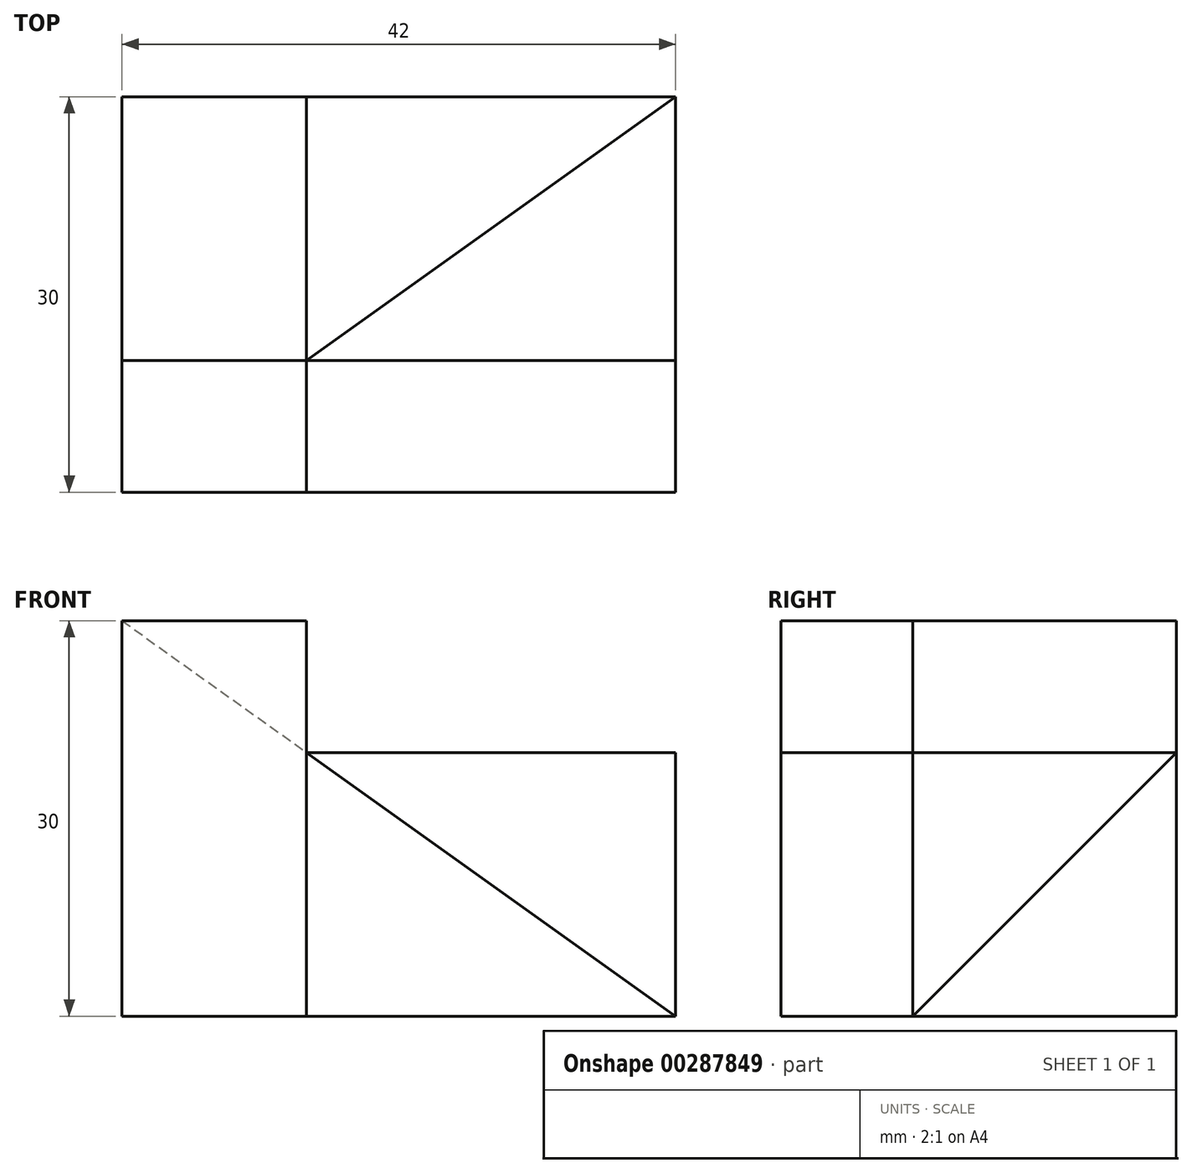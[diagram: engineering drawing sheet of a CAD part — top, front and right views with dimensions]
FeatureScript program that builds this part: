
annotation { "Feature Type Name" : "Feature", "Feature Type Description" : "" }
export const myFeature = defineFeature(function(context is Context, id is Id, definition is map)
    precondition{}
    {
        {
            var Q0;
            Q0=qCreatedBy(makeId("Front.planeOp"),FACE);
            var sketch = newSketch(context, id + "F0", { "sketchPlane" : qUnion([Q0])});
            skLineSegment(sketch, "E0.bottom", {"start": v(0, 0) * mm, "end": v(42, 0) * mm});
            skLineSegment(sketch, "E0.top", {"start": v(0, 30) * mm, "end": v(42, 30) * mm});
            skLineSegment(sketch, "E0.left", {"start": v(0, 0) * mm, "end": v(0, 30) * mm});
            skLineSegment(sketch, "E0.right", {"start": v(42, 0) * mm, "end": v(42, 30) * mm});
            skLineSegment(sketch, "E1.bottom", {"start": v(42, 30) * mm, "end": v(14, 30) * mm});
            skLineSegment(sketch, "E1.top", {"start": v(42, 20) * mm, "end": v(14, 20) * mm});
            skLineSegment(sketch, "E1.left", {"start": v(42, 30) * mm, "end": v(42, 20) * mm});
            skLineSegment(sketch, "E1.right", {"start": v(14, 30) * mm, "end": v(14, 20) * mm});
            skSolve(sketch);
        }
        {
            var Q0;
            Q0=makeQuery(id+"F0.imprint","IMPRINT",FACE,{"disambiguationData":[TD([[makeQuery(id+"F0.imprint","IMPRINT",EDGE,{"derivedFrom":sQuery(id+"F0.wireOp",EDGE,"E0.bottom")}),1.0]])]});
            extrude(context, id + "F1", {"entities" : qUnion([Q0]), "depth" : 30 * mm});
        }
        {
            var Q0;
            Q0=makeQuery(id+"F1.opExtrude","CAP_FACE",FACE,{"disambiguationData":[OSD([sQuery(id+"F0.wireOp",EDGE,"E0.bottom"),sQuery(id+"F0.wireOp",EDGE,"E0.top"),sQuery(id+"F0.wireOp",EDGE,"E0.left"),sQuery(id+"F0.wireOp",EDGE,"E0.right"),sQuery(id+"F0.wireOp",EDGE,"E1.top"),sQuery(id+"F0.wireOp",EDGE,"E1.right")])],"isStart":true});
            var sketch = newSketch(context, id + "F2", { "sketchPlane" : qUnion([Q0])});
            skLineSegment(sketch, "E2", {"start": v(0, 30) * mm, "end": v(-14, 20) * mm});
            skSolve(sketch);
        }
        {
            var Q0;
            Q0=makeQuery(id+"F2.imprint","IMPRINT",FACE,{"disambiguationData":[TD([[makeQuery(id+"F2.imprint","IMPRINT",EDGE,{"derivedFrom":sQuery(id+"F2.wireOp",EDGE,"E2")}),-1.0]])]});
            extrude(context, id + "F3", {"entities" : qUnion([Q0]), "operationType" : NewBodyOperationType.REMOVE, "flatOperationType" : FlatOperationType.REMOVE, "oppositeDirection" : true, "offsetDistance" : 25 * mm, "depth" : 20 * mm, "domain" : OperationDomain.MODEL});
        }
        {
            var Q0;
            Q0=makeQuery(id+"F1.opExtrude","CAP_FACE",FACE,{"disambiguationData":[OSD([sQuery(id+"F0.wireOp",EDGE,"E0.bottom"),sQuery(id+"F0.wireOp",EDGE,"E0.top"),sQuery(id+"F0.wireOp",EDGE,"E0.left"),sQuery(id+"F0.wireOp",EDGE,"E0.right"),sQuery(id+"F0.wireOp",EDGE,"E1.top"),sQuery(id+"F0.wireOp",EDGE,"E1.right")])],"isStart":false});
            var sketch = newSketch(context, id + "F4", { "sketchPlane" : qUnion([Q0])});
            skLineSegment(sketch, "E3", {"start": v(14, 20) * mm, "end": v(42, 0) * mm});
            skLineSegment(sketch, "E4", {"start": v(14, 20) * mm, "end": v(14, 0) * mm});
            skSolve(sketch);
        }
        {
            var Q0;
            Q0=makeQuery(id+"F4.imprint","IMPRINT",FACE,{"disambiguationData":[TD([[makeQuery(id+"F4.imprint","IMPRINT",EDGE,{"derivedFrom":sQuery(id+"F4.wireOp",EDGE,"E3")}),1.0]])]});
            extrude(context, id + "F5", {"entities" : qUnion([Q0]), "operationType" : NewBodyOperationType.REMOVE, "flatOperationType" : FlatOperationType.REMOVE, "oppositeDirection" : true, "offsetDistance" : 25 * mm, "depth" : 10 * mm, "domain" : OperationDomain.MODEL});
        }
        {
            var Q0;
            {var subQ0=sQuery(id+"F0.wireOp",EDGE,"E1.right");var subQ1=sQuery(id+"F0.wireOp",EDGE,"E1.top");Q0=makeQuery(id+"F5.boolean.opBoolean","MERGE",VERTEX,{"derivedFrom":[makeQuery(id+"F3.boolean.opBoolean","COPY",VERTEX,{"derivedFrom":makeQuery(id+"F3.opExtrude","CAP_VERTEX",VERTEX,{"disambiguationData":[OSD([subQ1,subQ0,sQuery(id+"F2.wireOp",EDGE,"E2")])],"isStart":false})}),makeQuery(id+"F5.opExtrude","CAP_VERTEX",VERTEX,{"disambiguationData":[OSD([subQ1,subQ0,sQuery(id+"F4.wireOp",EDGE,"E3")])],"isStart":false})]});}
            var Q1;
            Q1=makeQuery(id+"F1.opExtrude","CAP_VERTEX",VERTEX,{"disambiguationData":[OSD([sQuery(id+"F0.wireOp",EDGE,"E0.right"),sQuery(id+"F0.wireOp",EDGE,"E1.top"),sQuery(id+"F0.wireOp",EDGE,"E1.left")])],"isStart":true});
            var Q2;
            Q2=makeQuery(id+"F5.boolean.opBoolean","COPY",VERTEX,{"derivedFrom":makeQuery(id+"F5.opExtrude","CAP_VERTEX",VERTEX,{"disambiguationData":[OSD([sQuery(id+"F0.wireOp",EDGE,"E0.bottom"),sQuery(id+"F0.wireOp",EDGE,"E0.right"),sQuery(id+"F4.wireOp",EDGE,"E3")])],"isStart":false})});
            cPlane(context, id + "F6", {"entities" : qUnion([Q0, Q1, Q2]), "cplaneType" : CPlaneType.THREE_POINT, "offset" : 25 * mm, "width" : 150 * mm, "height" : 150 * mm});
        }
        {
            var Q0;
            Q0=qCreatedBy(id+"F6.planeOp",FACE);
            var sketch = newSketch(context, id + "F7", { "sketchPlane" : qUnion([Q0])});
            skPoint(sketch, "E5.0", {"position": v(-0.26, 0) * mm});
            skPoint(sketch, "E6.0", {"position": v(31.11, 14.14) * mm});
            skPoint(sketch, "E7.0", {"position": v(31.11, -14.14) * mm});
            skLineSegment(sketch, "E8", {"start": v(-0.26, 0) * mm, "end": v(31.11, 14.14) * mm});
            skLineSegment(sketch, "E9", {"start": v(31.11, -14.14) * mm, "end": v(31.11, 14.14) * mm});
            skLineSegment(sketch, "E10", {"start": v(-0.26, 0) * mm, "end": v(31.11, -14.14) * mm});
            skSolve(sketch);
        }
        {
            var Q0;
            Q0 = qSketchRegion(id + "F7", true);
            extrude(context, id + "F8", {"entities" : qUnion([Q0]), "operationType" : NewBodyOperationType.REMOVE, "endBound" : BoundingType.THROUGH_ALL, "depth" : 25 * mm});
        }
        {
            var Q0;
            Q0 = qSketchRegion(id + "F4", true);
            var Q1;
            Q1=makeQuery(id+"F4.imprint","IMPRINT",FACE,{"disambiguationData":[TD([[makeQuery(id+"F4.imprint","IMPRINT",EDGE,{"derivedFrom":sQuery(id+"F4.wireOp",EDGE,"E3")}),1.0]])]});
            var Q2;
            {var subQ0=sQuery(id+"F0.wireOp",EDGE,"E1.right");var subQ1=sQuery(id+"F0.wireOp",EDGE,"E1.top");Q2=makeQuery(id+"F8.boolean.opBoolean","MERGE",VERTEX,{"derivedFrom":[makeQuery(id+"F5.boolean.opBoolean","MERGE",VERTEX,{"derivedFrom":[makeQuery(id+"F3.boolean.opBoolean","COPY",VERTEX,{"derivedFrom":makeQuery(id+"F3.opExtrude","CAP_VERTEX",VERTEX,{"disambiguationData":[OSD([subQ1,subQ0,sQuery(id+"F2.wireOp",EDGE,"E2")])],"isStart":false})}),makeQuery(id+"F5.opExtrude","CAP_VERTEX",VERTEX,{"disambiguationData":[OSD([subQ1,subQ0,sQuery(id+"F4.wireOp",EDGE,"E3"),sQuery(id+"F4.wireOp",EDGE,"E4")])],"isStart":false})]}),makeQuery(id+"F8.opExtrude","CAP_VERTEX",VERTEX,{"disambiguationData":[OSD([sQuery(id+"F7.wireOp",EDGE,"E8"),sQuery(id+"F7.wireOp",EDGE,"E10")])],"isStart":true})]});}
            extrude(context, id + "F9", {"entities" : qUnion([Q0, Q1]), "operationType" : NewBodyOperationType.ADD, "endBound" : BoundingType.UP_TO_VERTEX, "oppositeDirection" : true, "endBoundEntityVertex" : qUnion([Q2]), "depth" : 25 * mm});
        }
        {
            var Q0;
            {var subQ0=sQuery(id+"F4.wireOp",EDGE,"E3");Q0=makeQuery(id+"F4.imprint","IMPRINT",FACE,{"disambiguationData":[TD([[makeQuery(id+"F4.imprint","IMPRINT",EDGE,{"derivedFrom":subQ0}),-1.0]])]});}
            var Q1;
            {var subQ0=sQuery(id+"F4.wireOp",EDGE,"E4");var subQ1=sQuery(id+"F4.wireOp",EDGE,"E3");var subQ2=sQuery(id+"F0.wireOp",EDGE,"E1.right");var subQ3=sQuery(id+"F0.wireOp",EDGE,"E1.top");Q1=makeQuery(id+"F9.boolean.opBoolean","MERGE",VERTEX,{"derivedFrom":[makeQuery(id+"F8.boolean.opBoolean","MERGE",VERTEX,{"derivedFrom":[makeQuery(id+"F5.boolean.opBoolean","MERGE",VERTEX,{"derivedFrom":[makeQuery(id+"F3.boolean.opBoolean","COPY",VERTEX,{"derivedFrom":makeQuery(id+"F3.opExtrude","CAP_VERTEX",VERTEX,{"disambiguationData":[OSD([subQ3,subQ2,sQuery(id+"F2.wireOp",EDGE,"E2")])],"isStart":false})}),makeQuery(id+"F5.opExtrude","CAP_VERTEX",VERTEX,{"disambiguationData":[OSD([subQ3,subQ2,subQ1,subQ0])],"isStart":false})]}),makeQuery(id+"F8.opExtrude","CAP_VERTEX",VERTEX,{"disambiguationData":[OSD([sQuery(id+"F7.wireOp",EDGE,"E8"),sQuery(id+"F7.wireOp",EDGE,"E10")])],"isStart":true})]}),makeQuery(id+"F9.opExtrude","CAP_VERTEX",VERTEX,{"disambiguationData":[OSD([subQ3,subQ2,subQ1,subQ0,dummyQuery(id+"F9.vertexPlane.planeOp",FACE)])],"isStart":false})]});}
            extrude(context, id + "F10", {"entities" : qUnion([Q0]), "operationType" : NewBodyOperationType.REMOVE, "endBound" : BoundingType.UP_TO_VERTEX, "oppositeDirection" : true, "endBoundEntityVertex" : qUnion([Q1]), "depth" : 25 * mm});
        }
    });
